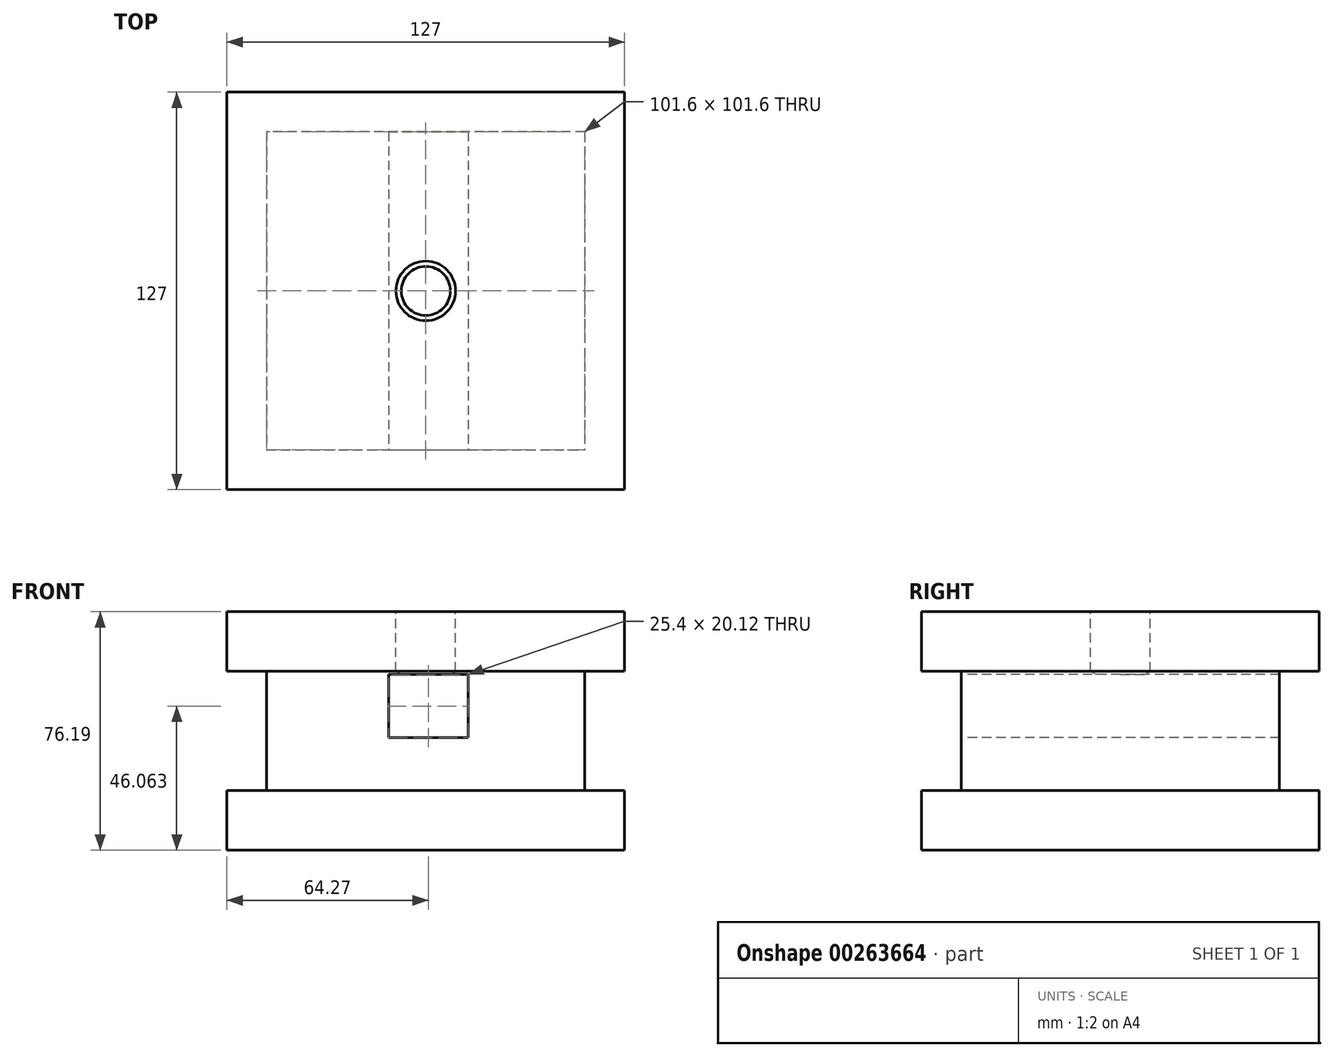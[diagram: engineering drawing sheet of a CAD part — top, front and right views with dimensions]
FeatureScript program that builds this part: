
annotation { "Feature Type Name" : "Feature", "Feature Type Description" : "" }
export const myFeature = defineFeature(function(context is Context, id is Id, definition is map)
    precondition{}
    {
        {
            var Q0;
            Q0=qCreatedBy(makeId("Front.planeOp"),FACE);
            var sketch = newSketch(context, id + "F0", { "sketchPlane" : qUnion([Q0])});
            skLineSegment(sketch, "E0", {"start": v(-51.57, 27.96) * mm, "end": v(75.43, 27.96) * mm});
            skLineSegment(sketch, "E1", {"start": v(75.43, 27.96) * mm, "end": v(75.43, 8.91) * mm});
            skLineSegment(sketch, "E2", {"start": v(75.43, 8.91) * mm, "end": v(62.73, 8.91) * mm});
            skLineSegment(sketch, "E3", {"start": v(62.73, 8.91) * mm, "end": v(62.73, -29.18) * mm});
            skLineSegment(sketch, "E4", {"start": v(62.73, -29.18) * mm, "end": v(75.43, -29.18) * mm});
            skLineSegment(sketch, "E5", {"start": v(75.43, -29.18) * mm, "end": v(75.43, -48.23) * mm});
            skLineSegment(sketch, "E6", {"start": v(75.43, -48.23) * mm, "end": v(-51.57, -48.23) * mm});
            skLineSegment(sketch, "E7", {"start": v(-51.57, -48.23) * mm, "end": v(-51.57, -29.18) * mm});
            skLineSegment(sketch, "E8", {"start": v(-51.57, -29.18) * mm, "end": v(-38.87, -29.18) * mm});
            skLineSegment(sketch, "E9", {"start": v(-38.87, -29.18) * mm, "end": v(-38.87, 8.91) * mm});
            skLineSegment(sketch, "E10", {"start": v(-38.87, 8.91) * mm, "end": v(-51.57, 8.91) * mm});
            skLineSegment(sketch, "E11", {"start": v(-51.57, 8.91) * mm, "end": v(-51.57, 27.96) * mm});
            skLineSegment(sketch, "E12", {"start": v(-38.87, 8.91) * mm, "end": v(62.73, 8.91) * mm});
            skLineSegment(sketch, "E13", {"start": v(62.73, -29.18) * mm, "end": v(-38.87, -29.18) * mm});
            skSolve(sketch);
        }
        {
            var Q0;
            Q0=makeQuery(id+"F0.imprint","IMPRINT",FACE,{"disambiguationData":[TD([[makeQuery(id+"F0.imprint","IMPRINT",EDGE,{"derivedFrom":sQuery(id+"F0.wireOp",EDGE,"E3")}),-1.0]])]});
            extrude(context, id + "F1", {"entities" : qUnion([Q0]), "oppositeDirection" : true, "depth" : 101.6 * mm});
        }
        {
            var Q0;
            Q0=makeQuery(id+"F0.imprint","IMPRINT",FACE,{"disambiguationData":[TD([[makeQuery(id+"F0.imprint","IMPRINT",EDGE,{"derivedFrom":sQuery(id+"F0.wireOp",EDGE,"E0")}),-1.0]])]});
            var Q1;
            Q1=makeQuery(id+"F0.imprint","IMPRINT",FACE,{"disambiguationData":[TD([[makeQuery(id+"F0.imprint","IMPRINT",EDGE,{"derivedFrom":sQuery(id+"F0.wireOp",EDGE,"E4")}),-1.0]])]});
            extrude(context, id + "F2", {"entities" : qUnion([Q0, Q1]), "operationType" : NewBodyOperationType.ADD, "oppositeDirection" : true, "depth" : 114.3 * mm, "hasSecondDirection" : true, "secondDirectionOppositeDirection" : false, "secondDirectionDepth" : 12.7 * mm});
        }
        {
            var Q0;
            Q0=qCreatedBy(makeId("Front.planeOp"),FACE);
            var sketch = newSketch(context, id + "F3", { "sketchPlane" : qUnion([Q0])});
            skLineSegment(sketch, "E14", {"start": v(0, -12.23) * mm, "end": v(25.4, -12.23) * mm});
            skLineSegment(sketch, "E15", {"start": v(0, -12.23) * mm, "end": v(0, 7.9) * mm});
            skLineSegment(sketch, "E16", {"start": v(0, 7.9) * mm, "end": v(25.4, 7.9) * mm});
            skPoint(sketch, "E17.end.orphan", {"position": v(25.4, 7.27) * mm});
            skLineSegment(sketch, "E18.left", {"start": v(0, 7.9) * mm, "end": v(0, -12.23) * mm});
            skLineSegment(sketch, "E18.right", {"start": v(25.4, 7.9) * mm, "end": v(25.4, -12.23) * mm});
            skSolve(sketch);
        }
        {
            var Q0;
            Q0=makeQuery(id+"F3.imprint","IMPRINT",FACE,{"disambiguationData":[TD([[makeQuery(id+"F3.imprint","IMPRINT",EDGE,{"derivedFrom":sQuery(id+"F3.wireOp",EDGE,"E16")}),-1.0]])]});
            extrude(context, id + "F4", {"entities" : qUnion([Q0]), "operationType" : NewBodyOperationType.REMOVE, "endBound" : BoundingType.THROUGH_ALL, "oppositeDirection" : true, "depth" : 127 * mm});
        }
        {
            var Q0;
            Q0=makeQuery(id+"F2.opExtrude","SWEPT_FACE",FACE,{"disambiguationData":[OSD([sQuery(id+"F0.wireOp",EDGE,"E0")])]});
            var sketch = newSketch(context, id + "F5", { "sketchPlane" : qUnion([Q0])});
            skLineSegment(sketch, "E19", {"start": v(-51.57, 50.8) * mm, "end": v(11.93, 50.8) * mm});
            skPoint(sketch, "E19.endSnap0", {"position": v(11.93, -12.7) * mm});
            skSolve(sketch);
        }
        {
            var Q0;
            Q0=sQuery(id+"F5.wireOp",VERTEX,"E19.end");
            var Q1;
            Q1=makeQuery(id+"F1.opExtrude","SWEPT_BODY",BODY,{"disambiguationData":[OSD([sQuery(id+"F0.wireOp",EDGE,"E3"),sQuery(id+"F0.wireOp",EDGE,"E9"),sQuery(id+"F0.wireOp",EDGE,"E12"),sQuery(id+"F0.wireOp",EDGE,"E13")])]});
            hole(context, id + "F6", {"style" : HoleStyle.SIMPLE, "endStyle" : HoleEndStyle.BLIND, "holeDiameter" : 19.05 * mm, "holeDepth" : 19.05 * mm, "tappedDepth" : 12.7 * mm, "tapClearance" : 3, "startFromSketch" : true, "locations" : qUnion([Q0]), "scope" : qUnion([Q1])});
        }
    });
